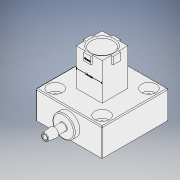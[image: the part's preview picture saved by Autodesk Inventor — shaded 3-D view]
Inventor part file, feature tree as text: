
AUTODESK INVENTOR PART (.ipt)
format: ipt  version: 2019 (Build 230136000, 136)  size: 619,520 bytes
history: native  units: mm
features: sketch x11, extrude x6, projected_geometry x4, plane x3, revolve x2, fillet x2, sweep x1, hole x1, pattern_circular x1
ambient origin geometry x8: Origin, YZ Plane, XZ Plane, XY Plane, X Axis, Y Axis, Z Axis, Center Point
bodies: Solid1 (feature_tree)
feature tree (31):
  revolve  "Revolution1"  [1 undecoded]
  plane  "Work Plane1"
  extrude  "Extrusion1"  Depth=0.35mm
  plane  "Work Plane7"
  extrude  "Extrusion6"  Depth=0.75mm
  extrude  "Extrusion7"  TaperAngle=90.0deg  [1 undecoded]
  sketch  "Sketch17"  dims[d11=0.0mm d14=2.0mm d15=0.0mm d45=0.0mm]
  plane  "Work Plane8"
  sweep  "Sweep3"
  fillet  "Fillet1"  [1 undecoded]
  hole  "Hole3"  [1 undecoded]
  revolve  "Revolution2"  [1 undecoded]
  fillet  "Fillet2"  Radius=32.7mm
  extrude  "Extrusion13"  Depth=3.0mm
  pattern_circular  "Circular Pattern1"  [2 undecoded]
  extrude  "Extrusion14"  Depth=6.0mm
  extrude  "Extrusion15"  Depth=5.0mm
  sketch  "Sketch1"  dims[d0=7.0mm d1=20.0mm]
  sketch  "Sketch2"  dims[d5=12.0mm d6=0.35mm]
  sketch  "Sketch11"  dims[d7=0.75mm d8=0.75mm]
  sketch  "Sketch16"  dims[d9=0.75mm d10=90.0deg]
  projected_geometry  "Projected Loop9"
  sketch  "Sketch18"  dims[d47=15.0mm d48=0.0mm d60=36.0mm]
  sketch  "Sketch19"  dims[d61=36.0mm d64=8.45mm d65=32.7mm d66=0.0mm]
  sketch  "Sketch21"  dims[d67=0.0mm d68=0.0mm d69=3.0mm]
  sketch  "Sketch28"  dims[d70=25.4mm]
  projected_geometry  "Projected Loop13"
  sketch  "Sketch30"  dims[d71=25.4mm]
  projected_geometry  "Projected Loop15"
  sketch  "Sketch31"  dims[d72=4.496mm d73=6.0mm d74=7.938mm d75=4.166mm d76=90.0deg d77=19.05mm d78=20.594885mm d79=3.0mm d80=6.0mm d81=5.0mm d82=1.8796mm d83=0.25mm d84=2.413mm d85=5.08mm d86=1.15mm d87=0.25mm d88=0.25mm d89=90.0deg d90=0.5mm d124=0.0mm d125=0.0mm d126=4.0mm d127=1.0mm d128=0.0mm d129=40.0mm d130=360.0deg d132=1.010217mm d133=0.5mm d134=0.0mm d135=0.5mm d136=0.0mm d137=1.0mm d138=0.125mm d139=0.125mm d140=0.125mm d141=4.75mm]
  projected_geometry  "Projected Loop16"
note: 7 required parameter values undecoded (feature->parameter linkage not recoverable at this tier; creation-order binding heuristic only, values carry confidence <= 0.55)